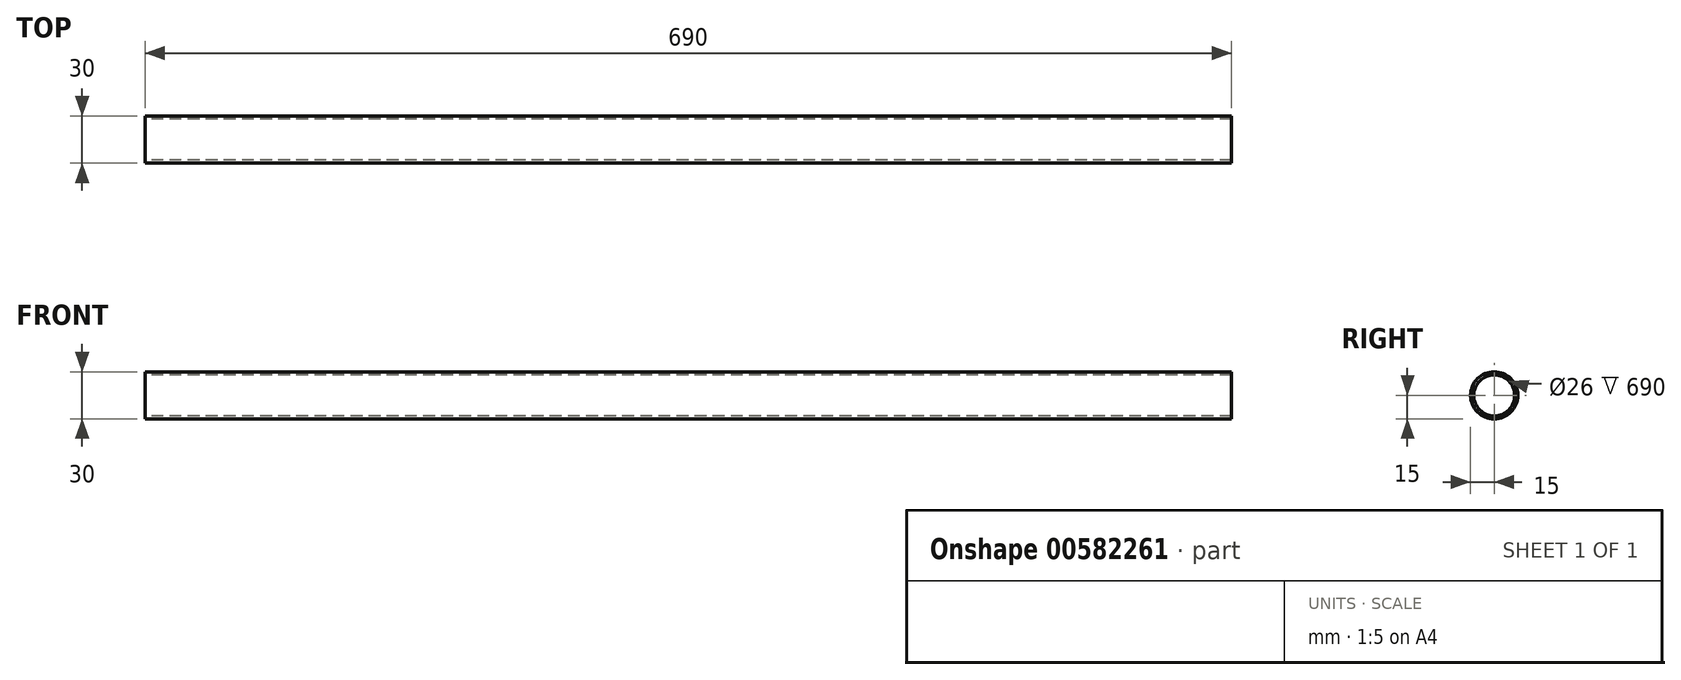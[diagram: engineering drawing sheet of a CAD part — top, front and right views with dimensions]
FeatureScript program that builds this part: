
annotation { "Feature Type Name" : "Feature", "Feature Type Description" : "" }
export const myFeature = defineFeature(function(context is Context, id is Id, definition is map)
    precondition{}
    {
        {
            var Q0;
            Q0=qCreatedBy(makeId("Right.planeOp"),FACE);
            var sketch = newSketch(context, id + "F0", { "sketchPlane" : qUnion([Q0])});
            skCircle(sketch, "E0", {"center": v(0, 0) * mm, "radius": 15 * mm});
            skCircle(sketch, "E1", {"center": v(0, 0) * mm, "radius": 13 * mm});
            skSolve(sketch);
        }
        {
            var Q0;
            Q0=makeQuery(id+"F0.imprint","IMPRINT",FACE,{"disambiguationData":[TD([[makeQuery(id+"F0.imprint","IMPRINT",EDGE,{"derivedFrom":sQuery(id+"F0.wireOp",EDGE,"E0")}),1.0]])]});
            extrude(context, id + "F1", {"entities" : qUnion([Q0]), "depth" : 690 * mm, "offsetDistance" : 25 * mm});
        }
    });
